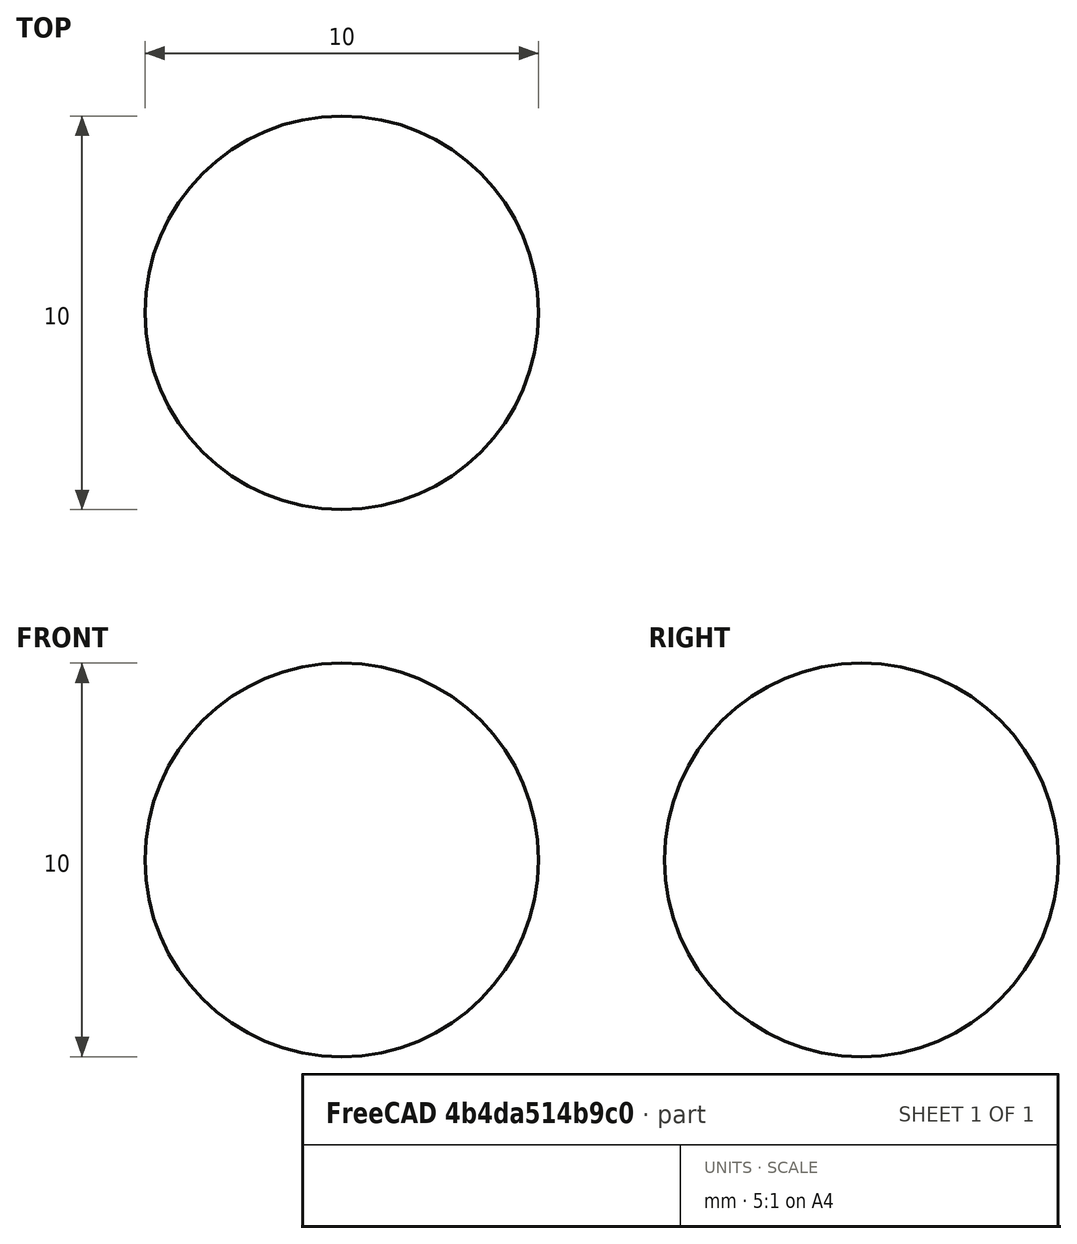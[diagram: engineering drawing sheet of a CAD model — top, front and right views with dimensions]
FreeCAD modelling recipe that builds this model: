
FCSTD DOCUMENT  (FreeCAD 0.19R17089 +1543 (Git))
Label: move
License: All rights reserved
LicenseURL: http://en.wikipedia.org/wiki/All_rights_reserved
objects: App::FeaturePython×10, Part::FeaturePython×10, App::Link×5, Sketcher::SketchObject×1, PartDesign::Revolution×1, PartDesign::Body×1, App::DocumentObjectGroup×1
note: 9 computed .brp shape members not serialized (recipe doc carries the construction recipe); baked Part::Feature solids carry a one-line shape summary decoded from their .brp

FEATURE [Sketcher::SketchObject] Sketch
  MapMode = 5
  Support = -> [XY_Plane]
  sketch-geometry (2):
    g0: ArcOfCircle CenterX=0 CenterY=0 CenterZ=0 NormalX=0 NormalY=0 NormalZ=1 AngleXU=0 Radius=5 StartAngle=0 EndAngle=3.14159
    g1: LineSegment StartX=-5 StartY=-1.6e-15 StartZ=0 EndX=5 EndY=1e-16 EndZ=0
  constraints (6):
    c: Coincident(g0,g-1)
    c: PointOnObject(g0,g-1)
    c: PointOnObject(g0,g-1)
    c: Radius(g0) = 5  'R1'
    c: Coincident(g1,g0)
    c: Coincident(g1,g0)
FEATURE [PartDesign::Revolution] Revolution
  Angle = 360
  Axis = (1,0,0)
  Base = (0,0,0)
  ClaimChildren = false
  Profile = -> Sketch
  ReferenceAxis = -> Sketch [H_Axis]
FEATURE [PartDesign::Body] Body
  Group = -> [Sketch,Revolution]
  Origin = -> Origin
  Tip = -> Revolution
FEATURE [App::FeaturePython] Constraints  # WARN: FeaturePython — macro-defined, semantics opaque (R4)
  GroupMode = 1
  _Version = 1
FEATURE [App::FeaturePython] Elements  # WARN: FeaturePython — macro-defined, semantics opaque (R4)
  GroupMode = 1
FEATURE [Part::FeaturePython] Parts  # WARN: FeaturePython — macro-defined, semantics opaque (R4)
  Group = -> [Body]
  GroupMode = 0
FEATURE [Part::FeaturePython] Assembly  label="Sphere"  # WARN: FeaturePython — macro-defined, semantics opaque (R4)
  AutoRelax = true
  BuildShape = 0
  Freeze = false
  Group = -> [Constraints,Elements,Parts]
  GroupMode = 1
  SolverType = 1
  Verbose = false
  _SolverType = 1
  _Version = 1
FEATURE [App::DocumentObjectGroup] Group  label="Repository"
  Group = -> [Assembly]
FEATURE [App::FeaturePython] Constraints001  # WARN: FeaturePython — macro-defined, semantics opaque (R4)
  GroupMode = 1
  _Version = 1
FEATURE [App::FeaturePython] Elements001  # WARN: FeaturePython — macro-defined, semantics opaque (R4)
  GroupMode = 1
FEATURE [App::FeaturePython] Constraints002  # WARN: FeaturePython — macro-defined, semantics opaque (R4)
  GroupMode = 1
  _Version = 1
FEATURE [App::FeaturePython] Elements002  # WARN: FeaturePython — macro-defined, semantics opaque (R4)
  GroupMode = 1
FEATURE [App::FeaturePython] Constraints003  # WARN: FeaturePython — macro-defined, semantics opaque (R4)
  GroupMode = 1
  _Version = 1
FEATURE [App::FeaturePython] Elements003  # WARN: FeaturePython — macro-defined, semantics opaque (R4)
  GroupMode = 1
FEATURE [App::FeaturePython] Constraints004  # WARN: FeaturePython — macro-defined, semantics opaque (R4)
  GroupMode = 1
  _Version = 1
FEATURE [App::FeaturePython] Elements004  # WARN: FeaturePython — macro-defined, semantics opaque (R4)
  GroupMode = 1
FEATURE [App::Link] Link  label="Sphere 1"
  LinkedObject = -> Assembly
FEATURE [App::Link] Link001  label="Sphere 2"
  LinkPlacement = pos=(0,0,-15) rot=(0,0,1;0rad)
  LinkedObject = -> Assembly
  Placement = pos=(0,0,-15) rot=(0,0,1;0rad)
FEATURE [App::Link] Link002  label="Sphere 3"
  LinkPlacement = pos=(0,0,-30) rot=(0,0,1;0rad)
  LinkedObject = -> Assembly
  Placement = pos=(0,0,-30) rot=(0,0,1;0rad)
FEATURE [App::Link] Link003  label="Sphere 4"
  LinkPlacement = pos=(0,0,-45) rot=(0,0,1;0rad)
  LinkedObject = -> Assembly
  Placement = pos=(0,0,-45) rot=(0,0,1;0rad)
FEATURE [App::Link] Link004  label="Sphere 4b"
  LinkPlacement = pos=(15,0,-45) rot=(0,0,1;0rad)
  LinkedObject = -> Assembly
  Placement = pos=(15,0,-45) rot=(0,0,1;0rad)
FEATURE [Part::FeaturePython] Parts004  # WARN: FeaturePython — macro-defined, semantics opaque (R4)
  Group = -> [Link003,Link004]
  GroupMode = 0
FEATURE [Part::FeaturePython] Assembly004  label="Level 4 Assembly"  # WARN: FeaturePython — macro-defined, semantics opaque (R4)
  AutoRelax = true
  BuildShape = 0
  Freeze = false
  Group = -> [Constraints004,Elements004,Parts004]
  GroupMode = 1
  SolverType = 1
  Verbose = false
  _SolverType = 1
  _Version = 1
FEATURE [Part::FeaturePython] Parts003  # WARN: FeaturePython — macro-defined, semantics opaque (R4)
  Group = -> [Assembly004,Link002]
  GroupMode = 0
FEATURE [Part::FeaturePython] Assembly003  label="Level 3 Assembly"  # WARN: FeaturePython — macro-defined, semantics opaque (R4)
  AutoRelax = true
  BuildShape = 0
  Freeze = false
  Group = -> [Constraints003,Elements003,Parts003]
  GroupMode = 1
  SolverType = 1
  Verbose = false
  _SolverType = 1
  _Version = 1
FEATURE [Part::FeaturePython] Parts002  # WARN: FeaturePython — macro-defined, semantics opaque (R4)
  Group = -> [Assembly003,Link001]
  GroupMode = 0
FEATURE [Part::FeaturePython] Assembly002  label="Level 2 Assembly"  # WARN: FeaturePython — macro-defined, semantics opaque (R4)
  AutoRelax = true
  BuildShape = 0
  Freeze = false
  Group = -> [Constraints002,Elements002,Parts002]
  GroupMode = 1
  SolverType = 1
  Verbose = false
  _SolverType = 1
  _Version = 1
FEATURE [Part::FeaturePython] Parts001  # WARN: FeaturePython — macro-defined, semantics opaque (R4)
  Group = -> [Assembly002,Link]
  GroupMode = 0
FEATURE [Part::FeaturePython] Assembly001  label="Project Assembly Container"  # WARN: FeaturePython — macro-defined, semantics opaque (R4)
  AutoRelax = true
  BuildShape = 0
  Freeze = false
  Group = -> [Constraints001,Elements001,Parts001]
  GroupMode = 1
  SolverType = 1
  Verbose = false
  _SolverType = 1
  _Version = 1
